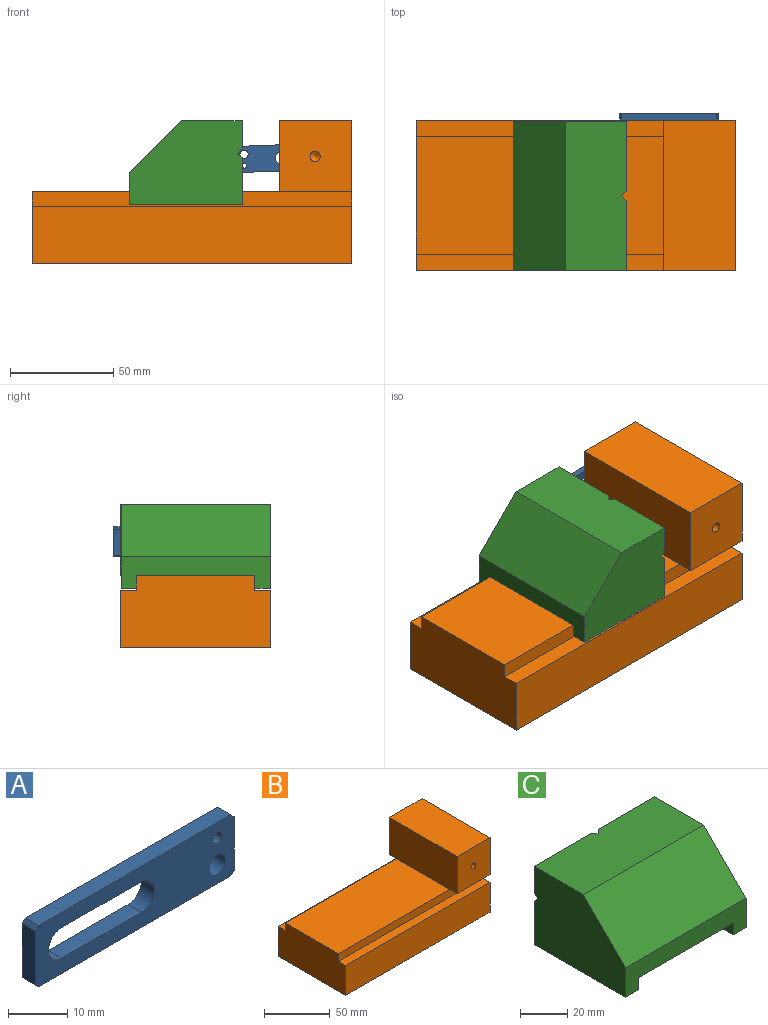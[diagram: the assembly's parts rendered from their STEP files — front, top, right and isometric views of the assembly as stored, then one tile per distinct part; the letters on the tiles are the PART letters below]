
ASSEMBLY  parts=3 mates=2
PART A: 16 faces, bbox 47.6x3.2x12.7 mm
  f0: plane 46.04x3.18mm, normal (0,0,-1), area 146.2mm2, adj f4,f5,f13,f14
  f1: plane 11.11x3.18mm, normal (1,0,0), area 35.3mm2, adj f4,f5,f14,f15
  f2: plane 46.04x3.18mm, normal (0,0,1), area 146.2mm2, adj f4,f5,f12,f15
  f3: plane 11.11x3.18mm, normal (-1,0,0), area 35.3mm2, adj f4,f5,f12,f13
  f4: plane 47.63x12.7mm, normal (0,-1,0), area 434.1mm2, adj f0,f1,f2,f3,f6,f7,f8,f9
  f5: plane 47.63x12.7mm, normal (0,1,0), area 434.1mm2, adj f0,f1,f2,f3,f6,f7,f8,f9
  f6: plane 19.05x3.18mm, normal (0,0,-1), area 60.5mm2, adj f4,f5,f7,f8
  f7: cylinder r=3.17mm len=6.35mm, axis (0,-1,0), area 31.7mm2, adj f4,f5,f6,f9
  f8: cylinder r=3.17mm len=6.35mm, axis (0,-1,0), area 31.7mm2, adj f4,f5,f6,f9
  f9: plane 19.05x3.18mm, normal (0,0,1), area 60.5mm2, adj f4,f5,f7,f8
  f10: cylinder r=1.13mm len=3.18mm, axis (0,-1,0), area 22.5mm2, adj f4,f5
  f11: cylinder r=2.02mm len=4.04mm, axis (0,-1,0), area 40.3mm2, adj f4,f5
  f12: plane 3.18x0.79mm, normal (-0.71,0,0.71), area 3.6mm2, adj f2,f3,f4,f5
  f13: plane 3.18x0.79mm, normal (-0.71,0,-0.71), area 3.6mm2, adj f0,f3,f4,f5
  f14: plane 3.18x0.79mm, normal (0.71,0,-0.71), area 3.6mm2, adj f0,f1,f4,f5
  f15: plane 3.18x0.79mm, normal (0.71,0,0.71), area 3.6mm2, adj f1,f2,f4,f5
PART B: 20 faces, bbox 154.9x72.9x69.3 mm
  f0: plane 72.9x34.87mm, normal (-1,0,0), area 2430.3mm2, adj f1,f2,f3,f5,f10,f12,f13,f14
  f1: plane 154.94x27.76mm, normal (0,1,0), area 4301.5mm2, adj f0,f4,f5,f13
  f2: plane 119.76x57.15mm, normal (0,0,1), area 6844.3mm2, adj f0,f7,f12,f14
  f3: plane 154.94x27.76mm, normal (0,-1,0), area 4301.5mm2, adj f0,f4,f5,f10
  f4: plane 72.9x69.34mm, normal (1,0,0), area 4942.9mm2, adj f1,f3,f5,f6,f8,f9,f10,f11
  f5: plane 154.94x72.9mm, normal (0,0,-1), area 11294.8mm2, adj f0,f1,f3,f4
  f6: plane 72.9x35.18mm, normal (0,0,1), area 2564.5mm2, adj f4,f7,f8,f9
  f7: plane 72.9x34.47mm, normal (-1,0,0), area 2512.6mm2, adj f2,f6,f8,f9,f11,f15
  f8: plane 35.18x34.47mm, normal (0,-1,0), area 1192.9mm2, adj f4,f6,f7,f11,f19
  f9: plane 35.18x34.47mm, normal (0,1,0), area 1192.9mm2, adj f4,f6,f7,f15,f17
  f10: plane 154.94x7.87mm, normal (0,0,1), area 1220mm2, adj f0,f3,f4,f12
  f11: plane 35.18x7.87mm, normal (0,0,-1), area 277mm2, adj f4,f7,f8,f12
  f12: plane 154.94x7.11mm, normal (0,-1,0), area 1101.9mm2, adj f0,f2,f4,f10,f11
  f13: plane 154.94x7.87mm, normal (0,0,1), area 1220mm2, adj f0,f1,f4,f14
  f14: plane 154.94x7.11mm, normal (0,1,0), area 1101.9mm2, adj f0,f2,f4,f13,f15
  f15: plane 35.18x7.87mm, normal (0,0,-1), area 277mm2, adj f4,f7,f9,f14
  f16: cone r=0mm half-angle=59deg, axis (0,1,0), area 22.9mm2, adj f17
  f17: cylinder r=2.5mm len=15.7mm, axis (0,1,0), area 246.6mm2, adj f9,f16
  f18: cone r=0mm half-angle=59deg, axis (0,-1,0), area 22.9mm2, adj f19
  f19: cylinder r=2.5mm len=15.7mm, axis (0,-1,0), area 246.6mm2, adj f8,f18
PART C: 22 faces, bbox 72.4x54.9x40.6 mm
  f0: plane 33.95x22.52mm, normal (0,1,0), area 597.4mm2, adj f1,f5,f10,f11,f16,f21
  f1: plane 54.86x40.64mm, normal (-1,0,0), area 1902.1mm2, adj f0,f8,f9,f11,f12,f15,f20,f21
  f2: plane 33.95x22.52mm, normal (0,1,0), area 597.4mm2, adj f3,f7,f10,f13,f17,f18
  f3: plane 54.86x40.64mm, normal (1,0,0), area 1902.1mm2, adj f2,f8,f12,f13,f14,f15,f18,f19
  f4: plane 15.88x2.25mm, normal (0.71,0.71,0), area 46.8mm2, adj f6,f8,f9,f20
  f5: plane 18.42x2.25mm, normal (0.71,0.71,0), area 54.9mm2, adj f0,f7,f10,f21
  f6: plane 15.88x2.25mm, normal (-0.71,0.71,0), area 46.8mm2, adj f4,f8,f14,f19
  f7: plane 18.42x2.25mm, normal (-0.71,0.71,0), area 54.9mm2, adj f2,f5,f10,f18
  f8: plane 72.39x29.46mm, normal (0,0,1), area 2127.9mm2, adj f1,f3,f4,f6,f9,f14,f15
  f9: plane 33.95x13.63mm, normal (0,1,0), area 462.7mm2, adj f1,f4,f8,f20
  f10: plane 57.15x54.86mm, normal (0,0,-1), area 3130.4mm2, adj f0,f2,f5,f7,f12,f16,f17
  f11: plane 54.86x7.62mm, normal (0,0,-1), area 418.1mm2, adj f0,f1,f12,f16
  f12: plane 72.39x15.24mm, normal (0,-1,0), area 740.3mm2, adj f1,f3,f10,f11,f13,f15,f16,f17
  f13: plane 54.86x7.62mm, normal (0,0,-1), area 418.1mm2, adj f2,f3,f12,f17
  f14: plane 33.95x13.63mm, normal (0,1,0), area 462.7mm2, adj f3,f6,f8,f19
  f15: plane 72.39x25.4mm, normal (0,-0.71,0.71), area 2600.3mm2, adj f1,f3,f8,f12
  f16: plane 54.86x6.35mm, normal (1,0,0), area 348.4mm2, adj f0,f10,f11,f12
  f17: plane 54.86x6.35mm, normal (-1,0,0), area 348.4mm2, adj f2,f10,f12,f13
  f18: plane 36.2x2.25mm, normal (0,0.71,0.71), area 111.4mm2, adj f2,f3,f7,f19
  f19: plane 36.2x2.25mm, normal (0,0.71,-0.71), area 111.4mm2, adj f3,f6,f14,f18
  f20: plane 36.2x2.25mm, normal (0,0.71,-0.71), area 111.4mm2, adj f1,f4,f9,f21
  f21: plane 36.2x2.25mm, normal (0,0.71,0.71), area 111.4mm2, adj f0,f1,f5,f20
PLACE A rot(axis=(0,1,0),177.8deg) t=(122.67,38.04,51.32)mm
PLACE B at identity fixed
PLACE C rot(axis=(0,0,-1),90deg) t=(101.78,-0.25,49.02)mm
MATE slider C.f14 <-> B.f7  axis (1,0,0) through (101.78,-36.45,69.34)mm
MATE pin_slot B.f16 <-> A.f8  axis (0,1,0) through (137.22,36.45,51.88)mm
